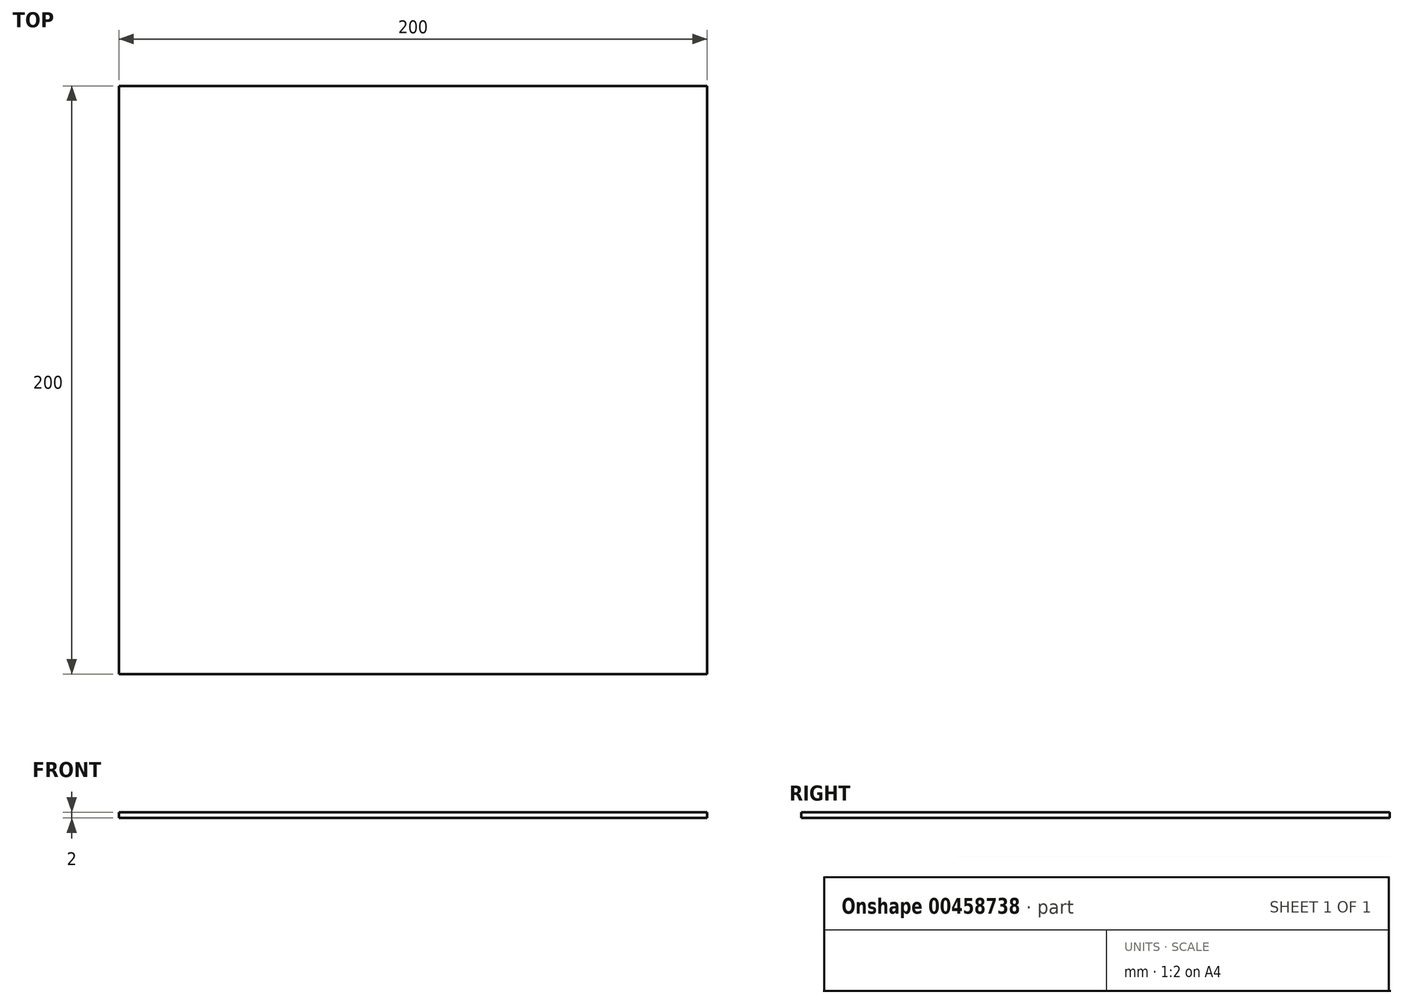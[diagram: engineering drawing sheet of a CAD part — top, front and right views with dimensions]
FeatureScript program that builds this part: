
annotation { "Feature Type Name" : "Feature", "Feature Type Description" : "" }
export const myFeature = defineFeature(function(context is Context, id is Id, definition is map)
    precondition{}
    {
        {
            var Q0;
            Q0=qCreatedBy(makeId("Top.planeOp"),FACE);
            var sketch = newSketch(context, id + "F0", { "sketchPlane" : qUnion([Q0])});
            skLineSegment(sketch, "E0.bottom", {"start": v(-100, 100) * mm, "end": v(100, 100) * mm});
            skLineSegment(sketch, "E0.top", {"start": v(-100, -100) * mm, "end": v(100, -100) * mm});
            skLineSegment(sketch, "E0.left", {"start": v(-100, 100) * mm, "end": v(-100, -100) * mm});
            skLineSegment(sketch, "E0.right", {"start": v(100, 100) * mm, "end": v(100, -100) * mm});
            skLineSegment(sketch, "E1", {"start": v(-100, 0) * mm, "end": v(100, 0) * mm, "construction": true});
            skSolve(sketch);
        }
        {
            var Q0;
            Q0 = qSketchRegion(id + "F0", true);
            extrude(context, id + "F1", {"entities" : qUnion([Q0]), "depth" : 2 * mm, "offsetDistance" : 25 * mm});
        }
    });
